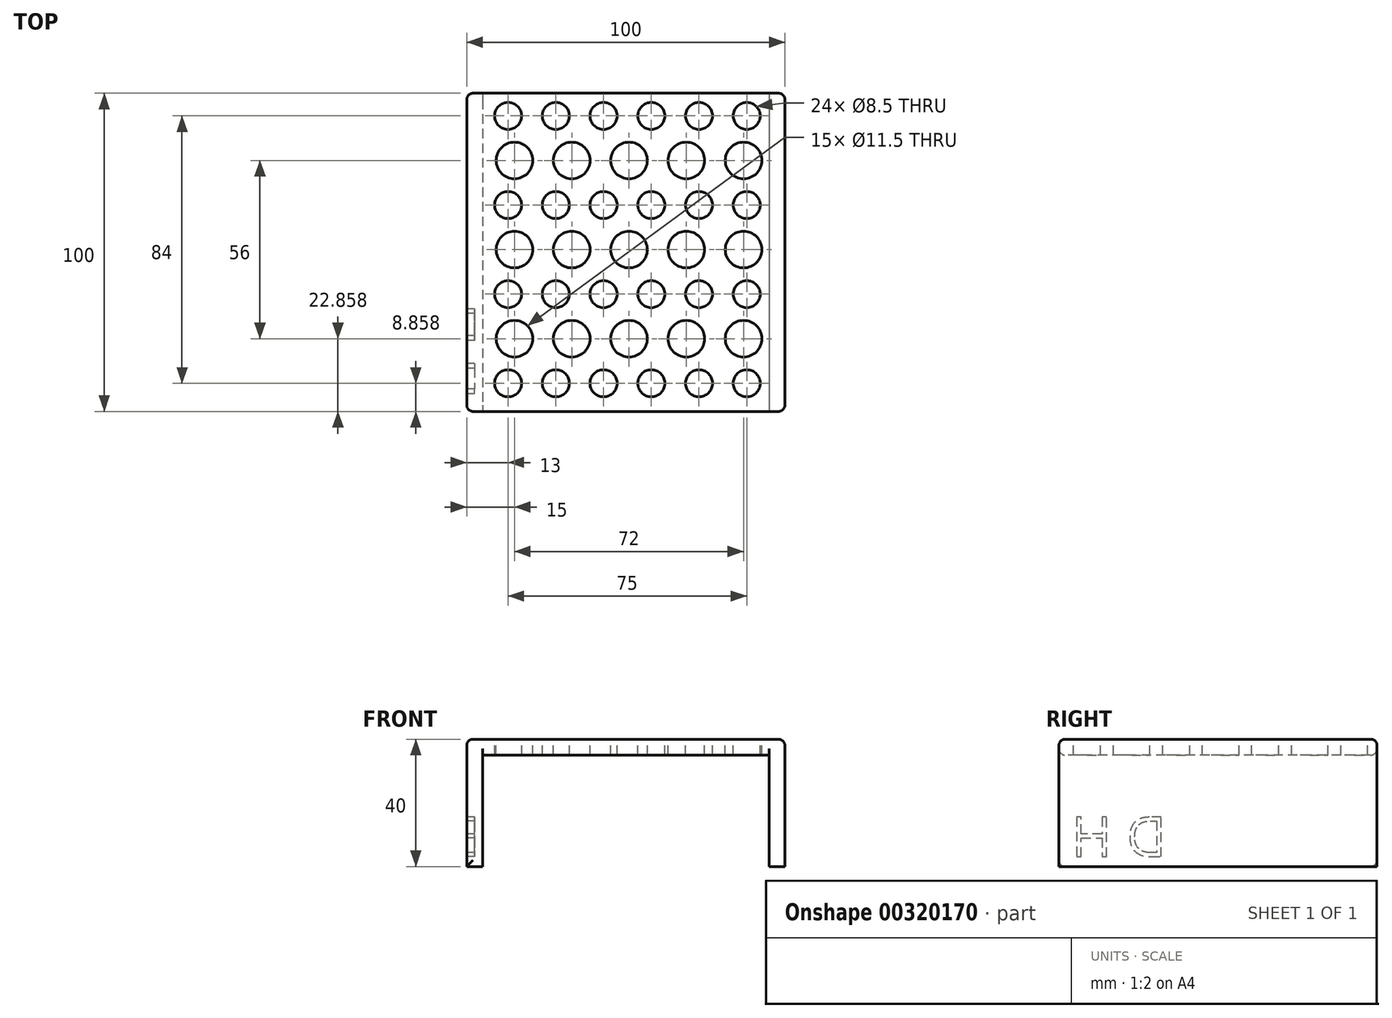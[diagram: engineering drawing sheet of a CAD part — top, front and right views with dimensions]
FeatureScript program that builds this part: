
annotation { "Feature Type Name" : "Feature", "Feature Type Description" : "" }
export const myFeature = defineFeature(function(context is Context, id is Id, definition is map)
    precondition{}
    {
        {
            var Q0;
            Q0=qCreatedBy(makeId("Top.planeOp"),FACE);
            var sketch = newSketch(context, id + "F0", { "sketchPlane" : qUnion([Q0])});
            skLineSegment(sketch, "E0.bottom", {"start": v(-50, 50) * mm, "end": v(50, 50) * mm});
            skLineSegment(sketch, "E0.top", {"start": v(-50, -50) * mm, "end": v(50, -50) * mm});
            skLineSegment(sketch, "E0.left", {"start": v(-50, 50) * mm, "end": v(-50, -50) * mm});
            skLineSegment(sketch, "E0.right", {"start": v(50, 50) * mm, "end": v(50, -50) * mm});
            skPoint(sketch, "E0.middle", {"position": v(0, 0) * mm});
            skLineSegment(sketch, "E1.top", {"start": v(-50, 40) * mm, "end": v(50, 40) * mm});
            skLineSegment(sketch, "E1.left", {"start": v(-50, 50) * mm, "end": v(-50, 40) * mm});
            skLineSegment(sketch, "E1.right", {"start": v(50, 50) * mm, "end": v(50, 40) * mm});
            skLineSegment(sketch, "E2.bottom", {"start": v(-50, -40) * mm, "end": v(50, -40) * mm});
            skLineSegment(sketch, "E2.left", {"start": v(-50, -40) * mm, "end": v(-50, -50) * mm});
            skLineSegment(sketch, "E2.right", {"start": v(50, -40) * mm, "end": v(50, -50) * mm});
            skSolve(sketch);
        }
        {
            var Q0;
            Q0=makeQuery(id+"F0.imprint","IMPRINT",FACE,{"disambiguationData":[TD([[makeQuery(id+"F0.imprint","IMPRINT",EDGE,{"derivedFrom":sQuery(id+"F0.wireOp",EDGE,"E0.left")}),1.0]])]});
            var Q1;
            Q1=makeQuery(id+"F0.imprint","IMPRINT",FACE,{"disambiguationData":[TD([[makeQuery(id+"F0.imprint","IMPRINT",EDGE,{"derivedFrom":sQuery(id+"F0.wireOp",EDGE,"E0.bottom")}),-1.0]])]});
            var Q2;
            Q2=makeQuery(id+"F0.imprint","IMPRINT",FACE,{"disambiguationData":[TD([[makeQuery(id+"F0.imprint","IMPRINT",EDGE,{"derivedFrom":sQuery(id+"F0.wireOp",EDGE,"E2.bottom")}),-1.0]])]});
            extrude(context, id + "F1", {"entities" : qUnion([Q0, Q1, Q2]), "depth" : 40 * mm});
        }
        {
            var Q0;
            Q0=makeQuery(id+"F1.opExtrude","SWEPT_FACE",FACE,{"disambiguationData":[OSD([sQuery(id+"F0.wireOp",EDGE,"E0.bottom")])]});
            var Q1;
            Q1=makeQuery(id+"F1.opExtrude","CAP_FACE",FACE,{"disambiguationData":[OSD([sQuery(id+"F0.wireOp",EDGE,"E0.left"),sQuery(id+"F0.wireOp",EDGE,"E0.right"),sQuery(id+"F0.wireOp",EDGE,"E0.bottom"),sQuery(id+"F0.wireOp",EDGE,"E1.left"),sQuery(id+"F0.wireOp",EDGE,"E1.right"),sQuery(id+"F0.wireOp",EDGE,"E0.top"),sQuery(id+"F0.wireOp",EDGE,"E2.left"),sQuery(id+"F0.wireOp",EDGE,"E2.right")])],"isStart":false});
            var Q2;
            Q2=makeQuery(id+"F1.opExtrude","SWEPT_FACE",FACE,{"disambiguationData":[OSD([sQuery(id+"F0.wireOp",EDGE,"E0.top")])]});
            shell(context, id + "F2", {"entities" : qUnion([Q0, Q1, Q2]), "thickness" : 5 * mm});
        }
        {
            var Q0;
            Q0=makeQuery(id+"F1.opExtrude","CAP_FACE",FACE,{"disambiguationData":[OSD([sQuery(id+"F0.wireOp",EDGE,"E0.left"),sQuery(id+"F0.wireOp",EDGE,"E0.right"),sQuery(id+"F0.wireOp",EDGE,"E0.bottom"),sQuery(id+"F0.wireOp",EDGE,"E1.left"),sQuery(id+"F0.wireOp",EDGE,"E1.right"),sQuery(id+"F0.wireOp",EDGE,"E0.top"),sQuery(id+"F0.wireOp",EDGE,"E2.left"),sQuery(id+"F0.wireOp",EDGE,"E2.right")])],"isStart":true});
            var sketch = newSketch(context, id + "F3", { "sketchPlane" : qUnion([Q0])});
            skCircle(sketch, "E3", {"center": v(-38, -42.86) * mm, "radius": 4.25 * mm});
            skCircle(sketch, "E4.0.1.0", {"center": v(-38, -14.86) * mm, "radius": 4.25 * mm});
            skCircle(sketch, "E4.0.2.0", {"center": v(-38, 13.14) * mm, "radius": 4.25 * mm});
            skCircle(sketch, "E4.0.3.0", {"center": v(-38, 41.14) * mm, "radius": 4.25 * mm});
            skCircle(sketch, "E4.1.0.0", {"center": v(-23, -42.86) * mm, "radius": 4.25 * mm});
            skCircle(sketch, "E4.1.1.0", {"center": v(-23, -14.86) * mm, "radius": 4.25 * mm});
            skCircle(sketch, "E4.1.2.0", {"center": v(-23, 13.14) * mm, "radius": 4.25 * mm});
            skCircle(sketch, "E4.1.3.0", {"center": v(-23, 41.14) * mm, "radius": 4.25 * mm});
            skCircle(sketch, "E4.2.0.0", {"center": v(-8, -42.86) * mm, "radius": 4.25 * mm});
            skCircle(sketch, "E4.2.1.0", {"center": v(-8, -14.86) * mm, "radius": 4.25 * mm});
            skCircle(sketch, "E4.2.2.0", {"center": v(-8, 13.14) * mm, "radius": 4.25 * mm});
            skCircle(sketch, "E4.2.3.0", {"center": v(-8, 41.14) * mm, "radius": 4.25 * mm});
            skCircle(sketch, "E4.3.0.0", {"center": v(7, -42.86) * mm, "radius": 4.25 * mm});
            skCircle(sketch, "E4.3.1.0", {"center": v(7, -14.86) * mm, "radius": 4.25 * mm});
            skCircle(sketch, "E4.3.2.0", {"center": v(7, 13.14) * mm, "radius": 4.25 * mm});
            skCircle(sketch, "E4.3.3.0", {"center": v(7, 41.14) * mm, "radius": 4.25 * mm});
            skCircle(sketch, "E4.4.0.0", {"center": v(22, -42.86) * mm, "radius": 4.25 * mm});
            skCircle(sketch, "E4.4.1.0", {"center": v(22, -14.86) * mm, "radius": 4.25 * mm});
            skCircle(sketch, "E4.4.2.0", {"center": v(22, 13.14) * mm, "radius": 4.25 * mm});
            skCircle(sketch, "E4.4.3.0", {"center": v(22, 41.14) * mm, "radius": 4.25 * mm});
            skCircle(sketch, "E4.5.0.0", {"center": v(37, -42.86) * mm, "radius": 4.25 * mm});
            skCircle(sketch, "E4.5.1.0", {"center": v(37, -14.86) * mm, "radius": 4.25 * mm});
            skCircle(sketch, "E4.5.2.0", {"center": v(37, 13.14) * mm, "radius": 4.25 * mm});
            skCircle(sketch, "E4.5.3.0", {"center": v(37, 41.14) * mm, "radius": 4.25 * mm});
            skLineSegment(sketch, "E4.direction1", {"start": v(-38, -42.86) * mm, "end": v(-23, -42.86) * mm, "construction": true});
            skLineSegment(sketch, "E4.direction2", {"start": v(-38, -42.86) * mm, "end": v(-38, -14.86) * mm, "construction": true});
            skCircle(sketch, "E5", {"center": v(-37, -28.86) * mm, "radius": 5.75 * mm});
            skCircle(sketch, "E6.0.1.0", {"center": v(-37, -0.86) * mm, "radius": 5.75 * mm});
            skCircle(sketch, "E6.0.2.0", {"center": v(-37, 27.14) * mm, "radius": 5.75 * mm});
            skCircle(sketch, "E6.1.0.0", {"center": v(-19, -28.86) * mm, "radius": 5.75 * mm});
            skCircle(sketch, "E6.1.1.0", {"center": v(-19, -0.86) * mm, "radius": 5.75 * mm});
            skCircle(sketch, "E6.1.2.0", {"center": v(-19, 27.14) * mm, "radius": 5.75 * mm});
            skCircle(sketch, "E6.2.0.0", {"center": v(-1, -28.86) * mm, "radius": 5.75 * mm});
            skCircle(sketch, "E6.2.1.0", {"center": v(-1, -0.86) * mm, "radius": 5.75 * mm});
            skCircle(sketch, "E6.2.2.0", {"center": v(-1, 27.14) * mm, "radius": 5.75 * mm});
            skCircle(sketch, "E6.3.0.0", {"center": v(17, -28.86) * mm, "radius": 5.75 * mm});
            skCircle(sketch, "E6.3.1.0", {"center": v(17, -0.86) * mm, "radius": 5.75 * mm});
            skCircle(sketch, "E6.3.2.0", {"center": v(17, 27.14) * mm, "radius": 5.75 * mm});
            skCircle(sketch, "E6.4.0.0", {"center": v(35, -28.86) * mm, "radius": 5.75 * mm});
            skCircle(sketch, "E6.4.1.0", {"center": v(35, -0.86) * mm, "radius": 5.75 * mm});
            skCircle(sketch, "E6.4.2.0", {"center": v(35, 27.14) * mm, "radius": 5.75 * mm});
            skLineSegment(sketch, "E6.direction1", {"start": v(-37, -28.86) * mm, "end": v(-19, -28.86) * mm, "construction": true});
            skLineSegment(sketch, "E6.direction2", {"start": v(-37, -28.86) * mm, "end": v(-37, -0.86) * mm, "construction": true});
            skSolve(sketch);
        }
        {
            var Q0;
            Q0=makeQuery(id+"F3.imprint","IMPRINT",FACE,{"disambiguationData":[TD([[makeQuery(id+"F3.imprint","IMPRINT",EDGE,{"derivedFrom":sQuery(id+"F3.wireOp",EDGE,"E4.3.2.0")}),1.0]])]});
            var Q1;
            Q1=makeQuery(id+"F3.imprint","IMPRINT",FACE,{"disambiguationData":[TD([[makeQuery(id+"F3.imprint","IMPRINT",EDGE,{"derivedFrom":sQuery(id+"F3.wireOp",EDGE,"E4.4.3.0")}),1.0]])]});
            var Q2;
            Q2=makeQuery(id+"F3.imprint","IMPRINT",FACE,{"disambiguationData":[TD([[makeQuery(id+"F3.imprint","IMPRINT",EDGE,{"derivedFrom":sQuery(id+"F3.wireOp",EDGE,"E4.3.1.0")}),1.0]])]});
            var Q3;
            Q3=makeQuery(id+"F3.imprint","IMPRINT",FACE,{"disambiguationData":[TD([[makeQuery(id+"F3.imprint","IMPRINT",EDGE,{"derivedFrom":sQuery(id+"F3.wireOp",EDGE,"E6.3.2.0")}),1.0]])]});
            var Q4;
            Q4=makeQuery(id+"F3.imprint","IMPRINT",FACE,{"disambiguationData":[TD([[makeQuery(id+"F3.imprint","IMPRINT",EDGE,{"derivedFrom":sQuery(id+"F3.wireOp",EDGE,"E6.4.1.0")}),1.0]])]});
            var Q5;
            Q5=makeQuery(id+"F3.imprint","IMPRINT",FACE,{"disambiguationData":[TD([[makeQuery(id+"F3.imprint","IMPRINT",EDGE,{"derivedFrom":sQuery(id+"F3.wireOp",EDGE,"E4.4.1.0")}),1.0]])]});
            var Q6;
            Q6=makeQuery(id+"F3.imprint","IMPRINT",FACE,{"disambiguationData":[TD([[makeQuery(id+"F3.imprint","IMPRINT",EDGE,{"derivedFrom":sQuery(id+"F3.wireOp",EDGE,"E6.3.0.0")}),1.0]])]});
            var Q7;
            Q7=makeQuery(id+"F3.imprint","IMPRINT",FACE,{"disambiguationData":[TD([[makeQuery(id+"F3.imprint","IMPRINT",EDGE,{"derivedFrom":sQuery(id+"F3.wireOp",EDGE,"E4.4.2.0")}),1.0]])]});
            var Q8;
            Q8=makeQuery(id+"F3.imprint","IMPRINT",FACE,{"disambiguationData":[TD([[makeQuery(id+"F3.imprint","IMPRINT",EDGE,{"derivedFrom":sQuery(id+"F3.wireOp",EDGE,"E6.3.1.0")}),1.0]])]});
            var Q9;
            Q9=makeQuery(id+"F3.imprint","IMPRINT",FACE,{"disambiguationData":[TD([[makeQuery(id+"F3.imprint","IMPRINT",EDGE,{"derivedFrom":sQuery(id+"F3.wireOp",EDGE,"E6.2.1.0")}),1.0]])]});
            var Q10;
            Q10=makeQuery(id+"F3.imprint","IMPRINT",FACE,{"disambiguationData":[TD([[makeQuery(id+"F3.imprint","IMPRINT",EDGE,{"derivedFrom":sQuery(id+"F3.wireOp",EDGE,"E4.0.3.0")}),1.0]])]});
            var Q11;
            Q11=makeQuery(id+"F3.imprint","IMPRINT",FACE,{"disambiguationData":[TD([[makeQuery(id+"F3.imprint","IMPRINT",EDGE,{"derivedFrom":sQuery(id+"F3.wireOp",EDGE,"E4.3.3.0")}),1.0]])]});
            var Q12;
            Q12=makeQuery(id+"F3.imprint","IMPRINT",FACE,{"disambiguationData":[TD([[makeQuery(id+"F3.imprint","IMPRINT",EDGE,{"derivedFrom":sQuery(id+"F3.wireOp",EDGE,"E4.5.1.0")}),1.0]])]});
            var Q13;
            Q13=makeQuery(id+"F3.imprint","IMPRINT",FACE,{"disambiguationData":[TD([[makeQuery(id+"F3.imprint","IMPRINT",EDGE,{"derivedFrom":sQuery(id+"F3.wireOp",EDGE,"E4.1.2.0")}),1.0]])]});
            var Q14;
            Q14=makeQuery(id+"F3.imprint","IMPRINT",FACE,{"disambiguationData":[TD([[makeQuery(id+"F3.imprint","IMPRINT",EDGE,{"derivedFrom":sQuery(id+"F3.wireOp",EDGE,"E6.4.2.0")}),1.0]])]});
            var Q15;
            Q15=makeQuery(id+"F3.imprint","IMPRINT",FACE,{"disambiguationData":[TD([[makeQuery(id+"F3.imprint","IMPRINT",EDGE,{"derivedFrom":sQuery(id+"F3.wireOp",EDGE,"E4.5.2.0")}),1.0]])]});
            var Q16;
            Q16=makeQuery(id+"F3.imprint","IMPRINT",FACE,{"disambiguationData":[TD([[makeQuery(id+"F3.imprint","IMPRINT",EDGE,{"derivedFrom":sQuery(id+"F3.wireOp",EDGE,"E4.1.3.0")}),1.0]])]});
            var Q17;
            Q17=makeQuery(id+"F3.imprint","IMPRINT",FACE,{"disambiguationData":[TD([[makeQuery(id+"F3.imprint","IMPRINT",EDGE,{"derivedFrom":sQuery(id+"F3.wireOp",EDGE,"E4.2.1.0")}),1.0]])]});
            var Q18;
            Q18=makeQuery(id+"F3.imprint","IMPRINT",FACE,{"disambiguationData":[TD([[makeQuery(id+"F3.imprint","IMPRINT",EDGE,{"derivedFrom":sQuery(id+"F3.wireOp",EDGE,"E4.2.2.0")}),1.0]])]});
            var Q19;
            Q19=makeQuery(id+"F3.imprint","IMPRINT",FACE,{"disambiguationData":[TD([[makeQuery(id+"F3.imprint","IMPRINT",EDGE,{"derivedFrom":sQuery(id+"F3.wireOp",EDGE,"E4.2.3.0")}),1.0]])]});
            var Q20;
            Q20=makeQuery(id+"F3.imprint","IMPRINT",FACE,{"disambiguationData":[TD([[makeQuery(id+"F3.imprint","IMPRINT",EDGE,{"derivedFrom":sQuery(id+"F3.wireOp",EDGE,"E4.3.0.0")}),1.0]])]});
            var Q21;
            Q21=makeQuery(id+"F3.imprint","IMPRINT",FACE,{"disambiguationData":[TD([[makeQuery(id+"F3.imprint","IMPRINT",EDGE,{"derivedFrom":sQuery(id+"F3.wireOp",EDGE,"E4.5.0.0")}),1.0]])]});
            var Q22;
            Q22=makeQuery(id+"F3.imprint","IMPRINT",FACE,{"disambiguationData":[TD([[makeQuery(id+"F3.imprint","IMPRINT",EDGE,{"derivedFrom":sQuery(id+"F3.wireOp",EDGE,"E6.4.0.0")}),1.0]])]});
            var Q23;
            Q23=makeQuery(id+"F3.imprint","IMPRINT",FACE,{"disambiguationData":[TD([[makeQuery(id+"F3.imprint","IMPRINT",EDGE,{"derivedFrom":sQuery(id+"F3.wireOp",EDGE,"E6.1.2.0")}),1.0]])]});
            var Q24;
            Q24=makeQuery(id+"F3.imprint","IMPRINT",FACE,{"disambiguationData":[TD([[makeQuery(id+"F3.imprint","IMPRINT",EDGE,{"derivedFrom":sQuery(id+"F3.wireOp",EDGE,"E4.4.0.0")}),1.0]])]});
            var Q25;
            Q25=makeQuery(id+"F3.imprint","IMPRINT",FACE,{"disambiguationData":[TD([[makeQuery(id+"F3.imprint","IMPRINT",EDGE,{"derivedFrom":sQuery(id+"F3.wireOp",EDGE,"E6.2.2.0")}),1.0]])]});
            var Q26;
            Q26=makeQuery(id+"F3.imprint","IMPRINT",FACE,{"disambiguationData":[TD([[makeQuery(id+"F3.imprint","IMPRINT",EDGE,{"derivedFrom":sQuery(id+"F3.wireOp",EDGE,"E4.5.3.0")}),1.0]])]});
            var Q27;
            Q27=makeQuery(id+"F3.imprint","IMPRINT",FACE,{"disambiguationData":[TD([[makeQuery(id+"F3.imprint","IMPRINT",EDGE,{"derivedFrom":sQuery(id+"F3.wireOp",EDGE,"E6.2.0.0")}),1.0]])]});
            var Q28;
            Q28=makeQuery(id+"F3.imprint","IMPRINT",FACE,{"disambiguationData":[TD([[makeQuery(id+"F3.imprint","IMPRINT",EDGE,{"derivedFrom":sQuery(id+"F3.wireOp",EDGE,"E4.0.1.0")}),1.0]])]});
            var Q29;
            Q29=makeQuery(id+"F3.imprint","IMPRINT",FACE,{"disambiguationData":[TD([[makeQuery(id+"F3.imprint","IMPRINT",EDGE,{"derivedFrom":sQuery(id+"F3.wireOp",EDGE,"E4.0.2.0")}),1.0]])]});
            var Q30;
            Q30=makeQuery(id+"F3.imprint","IMPRINT",FACE,{"disambiguationData":[TD([[makeQuery(id+"F3.imprint","IMPRINT",EDGE,{"derivedFrom":sQuery(id+"F3.wireOp",EDGE,"E6.1.1.0")}),1.0]])]});
            var Q31;
            Q31=makeQuery(id+"F3.imprint","IMPRINT",FACE,{"disambiguationData":[TD([[makeQuery(id+"F3.imprint","IMPRINT",EDGE,{"derivedFrom":sQuery(id+"F3.wireOp",EDGE,"E6.0.1.0")}),1.0]])]});
            var Q32;
            Q32=makeQuery(id+"F3.imprint","IMPRINT",FACE,{"disambiguationData":[TD([[makeQuery(id+"F3.imprint","IMPRINT",EDGE,{"derivedFrom":sQuery(id+"F3.wireOp",EDGE,"E4.1.0.0")}),1.0]])]});
            var Q33;
            Q33=makeQuery(id+"F3.imprint","IMPRINT",FACE,{"disambiguationData":[TD([[makeQuery(id+"F3.imprint","IMPRINT",EDGE,{"derivedFrom":sQuery(id+"F3.wireOp",EDGE,"E4.1.1.0")}),1.0]])]});
            var Q34;
            Q34=makeQuery(id+"F3.imprint","IMPRINT",FACE,{"disambiguationData":[TD([[makeQuery(id+"F3.imprint","IMPRINT",EDGE,{"derivedFrom":sQuery(id+"F3.wireOp",EDGE,"E4.2.0.0")}),1.0]])]});
            var Q35;
            Q35=makeQuery(id+"F3.imprint","IMPRINT",FACE,{"disambiguationData":[TD([[makeQuery(id+"F3.imprint","IMPRINT",EDGE,{"derivedFrom":sQuery(id+"F3.wireOp",EDGE,"E6.0.2.0")}),1.0]])]});
            var Q36;
            Q36=makeQuery(id+"F3.imprint","IMPRINT",FACE,{"disambiguationData":[TD([[makeQuery(id+"F3.imprint","IMPRINT",EDGE,{"derivedFrom":sQuery(id+"F3.wireOp",EDGE,"E6.1.0.0")}),1.0]])]});
            var Q37;
            Q37=makeQuery(id+"F3.imprint","IMPRINT",FACE,{"disambiguationData":[TD([[makeQuery(id+"F3.imprint","IMPRINT",EDGE,{"derivedFrom":sQuery(id+"F3.wireOp",EDGE,"E5")}),1.0]])]});
            var Q38;
            Q38=makeQuery(id+"F3.imprint","IMPRINT",FACE,{"disambiguationData":[TD([[makeQuery(id+"F3.imprint","IMPRINT",EDGE,{"derivedFrom":sQuery(id+"F3.wireOp",EDGE,"E3")}),1.0]])]});
            extrude(context, id + "F4", {"entities" : qUnion([Q0, Q1, Q2, Q3, Q4, Q5, Q6, Q7, Q8, Q9, Q10, Q11, Q12, Q13, Q14, Q15, Q16, Q17, Q18, Q19, Q20, Q21, Q22, Q23, Q24, Q25, Q26, Q27, Q28, Q29, Q30, Q31, Q32, Q33, Q34, Q35, Q36, Q37, Q38]), "operationType" : NewBodyOperationType.REMOVE, "endBound" : BoundingType.THROUGH_ALL, "oppositeDirection" : true, "depth" : 25 * mm});
        }
        {
            var Q0;
            Q0=makeQuery(id+"F1.opExtrude","CAP_EDGE",EDGE,{"disambiguationData":[OSD([sQuery(id+"F0.wireOp",EDGE,"E0.bottom")])],"isStart":true});
            var Q1;
            Q1=makeQuery(id+"F1.opExtrude","CAP_EDGE",EDGE,{"disambiguationData":[OSD([sQuery(id+"F0.wireOp",EDGE,"E0.left"),sQuery(id+"F0.wireOp",EDGE,"E1.left"),sQuery(id+"F0.wireOp",EDGE,"E2.left")])],"isStart":true});
            var Q2;
            Q2=makeQuery(id+"F1.opExtrude","CAP_EDGE",EDGE,{"disambiguationData":[OSD([sQuery(id+"F0.wireOp",EDGE,"E0.top")])],"isStart":true});
            var Q3;
            Q3=makeQuery(id+"F1.opExtrude","CAP_EDGE",EDGE,{"disambiguationData":[OSD([sQuery(id+"F0.wireOp",EDGE,"E0.right"),sQuery(id+"F0.wireOp",EDGE,"E1.right"),sQuery(id+"F0.wireOp",EDGE,"E2.right")])],"isStart":true});
            fillet(context, id + "F5", {"entities" : qUnion([Q0, Q1, Q2, Q3]), "radius" : 2 * mm, "tangentPropagation" : true, "allowEdgeOverflow" : false});
        }
        {
            var Q0;
            Q0=makeQuery(id+"F1.opExtrude","SWEPT_EDGE",EDGE,{"disambiguationData":[OSD([sQuery(id+"F0.wireOp",EDGE,"E0.bottom"),sQuery(id+"F0.wireOp",EDGE,"E1.left")])]});
            var Q1;
            Q1=makeQuery(id+"F2.opShell","OFFSET_EDGE",EDGE,{"disambiguationData":[OSD([sQuery(id+"F0.wireOp",EDGE,"E0.bottom"),sQuery(id+"F0.wireOp",EDGE,"E1.left")])]});
            var Q2;
            Q2=makeQuery(id+"F2.opShell","OFFSET_EDGE",EDGE,{"disambiguationData":[OSD([sQuery(id+"F0.wireOp",EDGE,"E0.bottom"),sQuery(id+"F0.wireOp",EDGE,"E1.right")])]});
            var Q3;
            Q3=makeQuery(id+"F1.opExtrude","SWEPT_EDGE",EDGE,{"disambiguationData":[OSD([sQuery(id+"F0.wireOp",EDGE,"E0.bottom"),sQuery(id+"F0.wireOp",EDGE,"E1.right")])]});
            var Q4;
            Q4=makeQuery(id+"F1.opExtrude","SWEPT_EDGE",EDGE,{"disambiguationData":[OSD([sQuery(id+"F0.wireOp",EDGE,"E0.top"),sQuery(id+"F0.wireOp",EDGE,"E2.right")])]});
            var Q5;
            {var subQ0=sQuery(id+"F0.wireOp",EDGE,"E0.top");Q5=makeQuery(id+"F5.opFillet","BLEND_EDGE",EDGE,{"blendedFrom":[makeQuery(id+"F1.opExtrude","CAP_EDGE",EDGE,{"disambiguationData":[OSD([subQ0])],"isStart":true}),makeQuery(id+"F1.opExtrude","CAP_FACE",FACE,{"disambiguationData":[OSD([sQuery(id+"F0.wireOp",EDGE,"E0.left"),sQuery(id+"F0.wireOp",EDGE,"E0.right"),sQuery(id+"F0.wireOp",EDGE,"E0.bottom"),sQuery(id+"F0.wireOp",EDGE,"E1.left"),sQuery(id+"F0.wireOp",EDGE,"E1.right"),subQ0,sQuery(id+"F0.wireOp",EDGE,"E2.left"),sQuery(id+"F0.wireOp",EDGE,"E2.right")])],"isStart":true})],"blendedInto":[makeQuery(id+"F1.opExtrude","CAP_FACE",FACE,{"disambiguationData":[OSD([sQuery(id+"F0.wireOp",EDGE,"E0.left"),sQuery(id+"F0.wireOp",EDGE,"E0.right"),sQuery(id+"F0.wireOp",EDGE,"E0.bottom"),sQuery(id+"F0.wireOp",EDGE,"E1.left"),sQuery(id+"F0.wireOp",EDGE,"E1.right"),subQ0,sQuery(id+"F0.wireOp",EDGE,"E2.left"),sQuery(id+"F0.wireOp",EDGE,"E2.right")])],"isStart":true})]});}
            var Q6;
            Q6=makeQuery(id+"F2.opShell","OFFSET_EDGE",EDGE,{"disambiguationData":[OSD([sQuery(id+"F0.wireOp",EDGE,"E0.top"),sQuery(id+"F0.wireOp",EDGE,"E2.left")])]});
            var Q7;
            Q7=makeQuery(id+"F1.opExtrude","SWEPT_EDGE",EDGE,{"disambiguationData":[OSD([sQuery(id+"F0.wireOp",EDGE,"E0.top"),sQuery(id+"F0.wireOp",EDGE,"E2.left")])]});
            var Q8;
            {var subQ0=sQuery(id+"F0.wireOp",EDGE,"E0.top");Q8=makeQuery(id+"F5.opFillet","BLEND_EDGE",EDGE,{"blendedFrom":[makeQuery(id+"F1.opExtrude","CAP_EDGE",EDGE,{"disambiguationData":[OSD([subQ0])],"isStart":true}),makeQuery(id+"F1.opExtrude","SWEPT_FACE",FACE,{"disambiguationData":[OSD([subQ0])]})],"blendedInto":[makeQuery(id+"F1.opExtrude","SWEPT_FACE",FACE,{"disambiguationData":[OSD([subQ0])]})]});}
            var Q9;
            {var subQ0=sQuery(id+"F0.wireOp",EDGE,"E0.bottom");Q9=makeQuery(id+"F2.opShell","OFFSET_EDGE",EDGE,{"disambiguationData":[OSD([subQ0]),TDD([makeQuery(id+"F1.opExtrude","CAP_EDGE",EDGE,{"disambiguationData":[OSD([subQ0])],"isStart":true})])]});}
            var Q10;
            {var subQ0=sQuery(id+"F0.wireOp",EDGE,"E0.bottom");Q10=makeQuery(id+"F5.opFillet","BLEND_EDGE",EDGE,{"blendedFrom":[makeQuery(id+"F1.opExtrude","CAP_EDGE",EDGE,{"disambiguationData":[OSD([subQ0])],"isStart":true}),makeQuery(id+"F1.opExtrude","SWEPT_FACE",FACE,{"disambiguationData":[OSD([subQ0])]})],"blendedInto":[makeQuery(id+"F1.opExtrude","SWEPT_FACE",FACE,{"disambiguationData":[OSD([subQ0])]})]});}
            fillet(context, id + "F6", {"entities" : qUnion([Q0, Q1, Q2, Q3, Q4, Q5, Q6, Q7, Q8, Q9, Q10]), "radius" : 2 * mm, "tangentPropagation" : true, "allowEdgeOverflow" : false});
        }
        {
            var Q0;
            Q0=makeQuery(id+"F1.opExtrude","SWEPT_BODY",BODY,{"disambiguationData":[OSD([sQuery(id+"F0.wireOp",EDGE,"E0.left"),sQuery(id+"F0.wireOp",EDGE,"E0.right"),sQuery(id+"F0.wireOp",EDGE,"E0.bottom"),sQuery(id+"F0.wireOp",EDGE,"E1.left"),sQuery(id+"F0.wireOp",EDGE,"E1.right"),sQuery(id+"F0.wireOp",EDGE,"E0.top"),sQuery(id+"F0.wireOp",EDGE,"E2.left"),sQuery(id+"F0.wireOp",EDGE,"E2.right")])]});
            var Q1;
            {var subQ0=sQuery(id+"F0.wireOp",EDGE,"E2.left");var subQ1=sQuery(id+"F0.wireOp",EDGE,"E1.left");var subQ2=sQuery(id+"F0.wireOp",EDGE,"E0.left");Q1=makeQuery(id+"F2.opShell","OFFSET_EDGE",EDGE,{"disambiguationData":[OSD([subQ2,subQ1,subQ0]),TDD([makeQuery(id+"F1.opExtrude","CAP_EDGE",EDGE,{"disambiguationData":[OSD([subQ2,subQ1,subQ0])],"isStart":true})])]});}
            transform(context, id + "F7", {"entities" : qUnion([Q0]), "transformType" : TransformType.ROTATION, "transformAxis" : qUnion([Q1]), "angle" : 180 * degree, "makeCopy" : false});
        }
        {
            var Q0;
            Q0=makeQuery(id+"F1.opExtrude","SWEPT_FACE",FACE,{"disambiguationData":[OSD([sQuery(id+"F0.wireOp",EDGE,"E0.right"),sQuery(id+"F0.wireOp",EDGE,"E1.right"),sQuery(id+"F0.wireOp",EDGE,"E2.right")])]});
            var sketch = newSketch(context, id + "F8", { "sketchPlane" : qUnion([Q0])});
            skText(sketch, "E7", { "text": "D H", "fontName": "OpenSans-Regular.ttf"});
            const initialGuessF8  = {"E7": [0.01608, -0.0269, 1, 0, 0.01252]};
            skSetInitialGuess(sketch, initialGuessF8);
            skSolve(sketch);
        }
        {
            var Q0;
            Q0 = qSketchRegion(id + "F8", true);
            extrude(context, id + "F9", {"entities" : qUnion([Q0]), "operationType" : NewBodyOperationType.REMOVE, "oppositeDirection" : true, "depth" : 2.5 * mm});
        }
    });
